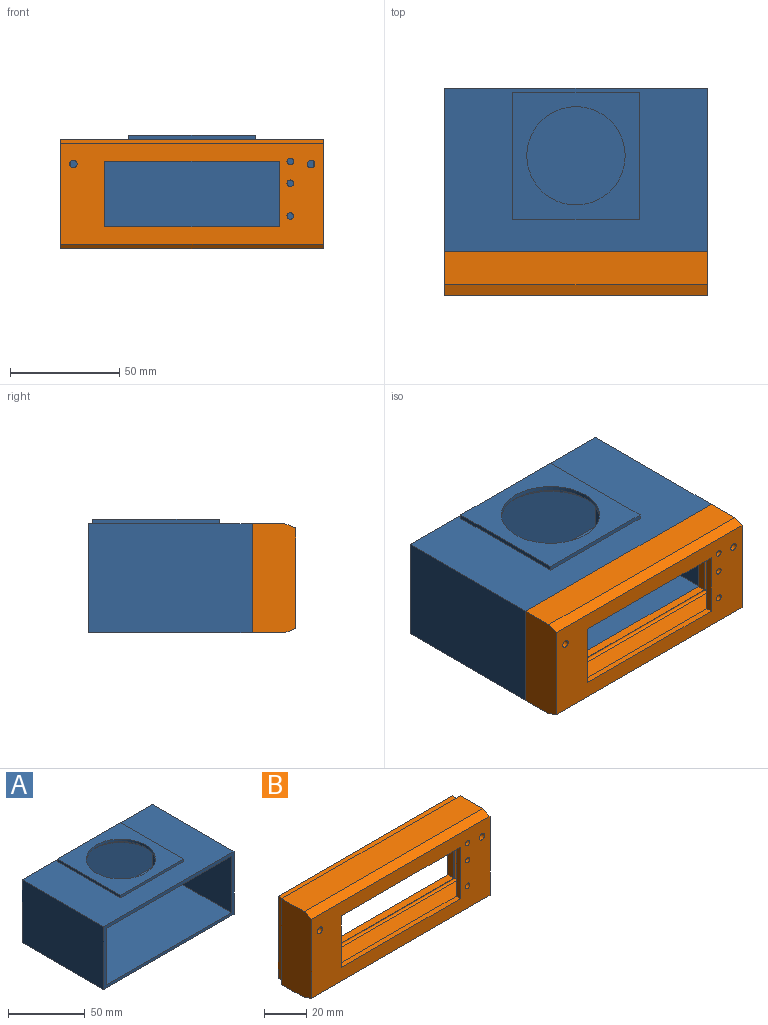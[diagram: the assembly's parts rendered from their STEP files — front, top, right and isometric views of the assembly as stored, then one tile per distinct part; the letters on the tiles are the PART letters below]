
ASSEMBLY  parts=2 mates=1
PART A: 19 faces, bbox 120x75x52 mm
  f0: plane 120x75mm, normal (0,0,1), area 5636mm2, adj f1,f3,f4,f5,f12,f13,f14,f16
  f1: plane 120x50mm, normal (0,-1,0), area 825mm2, adj f0,f2,f3,f4,f6,f7,f8,f9
  f2: plane 120x75mm, normal (0,0,-1), area 9000mm2, adj f1,f3,f4,f5
  f3: plane 75x50mm, normal (1,0,0), area 3750mm2, adj f0,f1,f2,f5
  f4: plane 75x50mm, normal (-1,0,0), area 3750mm2, adj f0,f1,f2,f5
  f5: plane 120x50mm, normal (0,1,0), area 6000mm2, adj f0,f2,f3,f4
  f6: plane 115x72.5mm, normal (0,0,1), area 8337.5mm2, adj f1,f7,f9,f10
  f7: plane 72.5x45mm, normal (-1,0,0), area 3262.5mm2, adj f1,f6,f8,f10
  f8: plane 115x72.5mm, normal (0,0,-1), area 6374mm2, adj f1,f7,f9,f10,f11
  f9: plane 72.5x45mm, normal (1,0,0), area 3262.5mm2, adj f1,f6,f8,f10
  f10: plane 115x45mm, normal (0,-1,0), area 5175mm2, adj f6,f7,f8,f9
  f11: cylinder r=25mm len=50mm, axis (0,0,1), area 392.7mm2, adj f8,f18
  f12: plane 58x2mm, normal (1,0,0), area 116mm2, adj f0,f13,f16,f17
  f13: plane 58x2mm, normal (0,1,0), area 116mm2, adj f0,f12,f14,f17
  f14: plane 58x2mm, normal (-1,0,0), area 116mm2, adj f0,f13,f16,f17
  f15: cylinder r=22.5mm len=45mm, axis (0,0,-1), area 282.7mm2, adj f17,f18
  f16: plane 58x2mm, normal (0,-1,0), area 116mm2, adj f0,f12,f14,f17
  f17: plane 58x58mm, normal (0,0,1), area 1773.6mm2, adj f12,f13,f14,f15,f16
  f18: plane 50x50mm, normal (0,0,-1), area 373.1mm2, adj f11,f15
PART B: 77 faces, bbox 120x24x50 mm
  f0: plane 112x42mm, normal (0,-1,0), area 74.1mm2, adj f1,f2,f3,f8,f73,f74,f75,f76
  f1: plane 111.18x4mm, normal (0,0,-1), area 444.7mm2, adj f0,f2,f8,f9
  f2: plane 41.64x4mm, normal (1,0,0), area 166.6mm2, adj f0,f1,f3,f9
  f3: plane 111.18x4mm, normal (0,0,1), area 444.7mm2, adj f0,f2,f8,f9
  f4: plane 47.64x4mm, normal (1,0,0), area 190.6mm2, adj f5,f7,f9,f20
  f5: plane 117.18x4mm, normal (0,0,-1), area 468.7mm2, adj f4,f6,f9,f20
  f6: plane 47.64x4mm, normal (-1,0,0), area 190.6mm2, adj f5,f7,f9,f20
  f7: plane 117.18x4mm, normal (0,0,1), area 468.7mm2, adj f4,f6,f9,f20
  f8: plane 41.64x4mm, normal (-1,0,0), area 166.6mm2, adj f0,f1,f3,f9
  f9: plane 117.18x47.64mm, normal (0,1,0), area 953mm2, adj f1,f2,f3,f4,f5,f6,f7,f8
  f10: plane 5.2x0.15mm, normal (0,0,-1), area 0.8mm2, adj f13,f39,f54,f68
  f11: cylinder r=2mm len=5.2mm, axis (0,-1,0), area 11.5mm2, adj f12,f38,f39,f68
  f12: torus R=4mm, axis (0,-1,0), area 13mm2, adj f11,f13,f28,f50,f68
  f13: cylinder r=2mm len=2mm, axis (-1,0,0), area 2.6mm2, adj f10,f12,f28,f56,f68
  f14: plane 5.2x1.96mm, normal (0,0,-1), area 10.2mm2, adj f15,f27,f34,f67
  f15: cylinder r=2mm len=3mm, axis (-1,0,0), area 8.8mm2, adj f14,f17,f27,f28,f67
  f16: cylinder r=2mm len=5.2mm, axis (0,-1,0), area 14mm2, adj f17,f33,f34,f67
  f17: torus R=4mm, axis (0,-1,0), area 13.3mm2, adj f15,f16,f28,f43,f67
  f18: plane 44.4x14mm, normal (1,0,0), area 507.2mm2, adj f19,f26,f39,f41,f42,f54,f59,f76
  f19: plane 114.4x14mm, normal (0,0,-1), area 1539.2mm2, adj f18,f27,f33,f34,f39,f44,f45,f74
  f20: plane 120x50mm, normal (0,1,0), area 417.1mm2, adj f4,f5,f6,f7,f21,f22,f23,f24
  f21: plane 120x15mm, normal (0,0,-1), area 1800mm2, adj f20,f22,f24,f63
  f22: plane 50x20mm, normal (1,0,0), area 990mm2, adj f20,f21,f23,f25,f62,f63
  f23: plane 120x15mm, normal (0,0,1), area 1800mm2, adj f20,f22,f24,f62
  f24: plane 50x20mm, normal (-1,0,0), area 990mm2, adj f20,f21,f23,f25,f62,f63
  f25: plane 120x46mm, normal (0,-1,0), area 3079.6mm2, adj f22,f24,f29,f30,f31,f32,f62,f63
  f26: plane 114.4x14mm, normal (0,0,1), area 1539.2mm2, adj f18,f27,f36,f37,f42,f52,f53,f75
  f27: plane 44.4x16mm, normal (-1,0,0), area 564.7mm2, adj f14,f15,f19,f26,f28,f34,f35,f37
  f28: plane 112.4x40.4mm, normal (0,1,0), area 1893.5mm2, adj f12,f13,f15,f17,f27,f29,f30,f31
  f29: plane 30x2.8mm, normal (-1,0,0), area 84mm2, adj f25,f28,f30,f32
  f30: plane 80x2.8mm, normal (0,0,-1), area 224mm2, adj f25,f28,f29,f31
  f31: plane 30x2.8mm, normal (1,0,0), area 84mm2, adj f25,f28,f30,f32
  f32: plane 80x2.8mm, normal (0,0,1), area 224mm2, adj f25,f28,f29,f31
  f33: plane 8x5.2mm, normal (-1,0,0), area 41.6mm2, adj f16,f19,f34,f43
  f34: plane 10x5mm, normal (0,1,0), area 39.7mm2, adj f14,f16,f19,f27,f33,f67
  f35: plane 5.2x3mm, normal (0,0,1), area 15.6mm2, adj f27,f37,f46,f47
  f36: plane 8x5.2mm, normal (-1,0,0), area 41.6mm2, adj f26,f37,f46,f51
  f37: plane 10x5mm, normal (0,1,0), area 39.5mm2, adj f26,f27,f35,f36,f46,f71
  f38: plane 6x5.2mm, normal (1,0,0), area 31.2mm2, adj f11,f39,f45,f50
  f39: plane 12x7mm, normal (0,1,0), area 41.4mm2, adj f10,f11,f18,f19,f38,f45,f54,f68
  f40: plane 6x5.2mm, normal (1,0,0), area 31.2mm2, adj f42,f52,f57,f58
  f41: plane 5.2x3mm, normal (0,0,1), area 15.6mm2, adj f18,f42,f57,f61
  f42: plane 10x7mm, normal (0,1,0), area 40.4mm2, adj f18,f26,f40,f41,f52,f57,f69
  f43: cylinder r=2mm len=8mm, axis (0,0,1), area 22.8mm2, adj f17,f28,f33,f44
  f44: cylinder r=2mm len=102.4mm, axis (-1,0,0), area 319.4mm2, adj f19,f28,f43,f48
  f45: cylinder r=2mm len=5.2mm, axis (0,-1,0), area 16.3mm2, adj f19,f38,f39,f48
  f46: cylinder r=2mm len=5.2mm, axis (0,-1,0), area 16.3mm2, adj f35,f36,f37,f49
  f47: cylinder r=2mm len=3mm, axis (1,0,0), area 9.4mm2, adj f27,f28,f35,f49
  f48: sphere r=2mm, area 6.3mm2, adj f44,f45,f50
  f49: torus R=4mm, axis (0,-1,0), area 13.5mm2, adj f28,f46,f47,f51
  f50: cylinder r=2mm len=6mm, axis (0,0,-1), area 18.8mm2, adj f12,f28,f38,f48
  f51: cylinder r=2mm len=8mm, axis (0,0,1), area 22.8mm2, adj f28,f36,f49,f53
  f52: cylinder r=2mm len=5.2mm, axis (0,-1,0), area 16.3mm2, adj f26,f40,f42,f55
  f53: cylinder r=2mm len=102.4mm, axis (1,0,0), area 319.4mm2, adj f26,f28,f51,f55
  f54: cylinder r=2mm len=5.2mm, axis (0,1,0), area 16.3mm2, adj f10,f18,f39,f56
  f55: sphere r=2mm, area 6.3mm2, adj f52,f53,f58
  f56: sphere r=2mm, area 6.3mm2, adj f13,f54,f59
  f57: cylinder r=2mm len=5.2mm, axis (0,-1,0), area 16.3mm2, adj f40,f41,f42,f60
  f58: cylinder r=2mm len=6mm, axis (0,0,-1), area 18.8mm2, adj f28,f40,f55,f60
  f59: cylinder r=2mm len=22.4mm, axis (0,0,-1), area 68.1mm2, adj f18,f28,f56,f61
  f60: torus R=4mm, axis (0,-1,0), area 13.5mm2, adj f28,f57,f58,f61
  f61: cylinder r=2mm len=3mm, axis (1,0,0), area 7.1mm2, adj f28,f41,f59,f60
  f62: plane 120x5mm, normal (0,-0.37,0.93), area 646.2mm2, adj f22,f23,f24,f25
  f63: plane 120x5mm, normal (0,-0.37,-0.93), area 646.2mm2, adj f21,f22,f24,f25
  f64: cylinder r=1.5mm len=3mm, axis (0,-1,0), area 26.4mm2, adj f25,f28
  f65: cylinder r=1.5mm len=3mm, axis (0,-1,0), area 26.4mm2, adj f25,f28
  f66: cylinder r=1.5mm len=3mm, axis (0,-1,0), area 26.4mm2, adj f25,f28
  f67: cylinder r=1.75mm len=10mm, axis (0,1,0), area 101.1mm2, adj f14,f15,f16,f17,f25,f34
  f68: cylinder r=1.75mm len=10mm, axis (0,1,0), area 99.3mm2, adj f10,f11,f12,f13,f25,f39
  f69: cylinder r=1.75mm len=5mm, axis (0,1,0), area 55mm2, adj f42,f70
  f70: cone r=0mm half-angle=59deg, axis (0,1,0), area 11.2mm2, adj f69
  f71: cylinder r=1.75mm len=5mm, axis (0,1,0), area 55mm2, adj f37,f72
  f72: cone r=0mm half-angle=59deg, axis (0,1,0), area 11.2mm2, adj f71
  f73: cylinder r=1.2mm len=44.4mm, axis (0,0,1), area 82mm2, adj f0,f27,f74,f75
  f74: cylinder r=1.2mm len=114.4mm, axis (-1,0,0), area 214mm2, adj f0,f19,f73,f76
  f75: cylinder r=1.2mm len=114.4mm, axis (1,0,0), area 214mm2, adj f0,f26,f73,f76
  f76: cylinder r=1.2mm len=44.4mm, axis (0,0,-1), area 82mm2, adj f0,f18,f74,f75
PLACE A t=(-72.13,-72.75,-5.41)mm
PLACE B t=(-72.13,-82.75,-5.41)mm fixed
MATE fastened A.f1 <-> B.f20  axis (0,-1,0) through (-132.13,-72.75,19.59)mm
